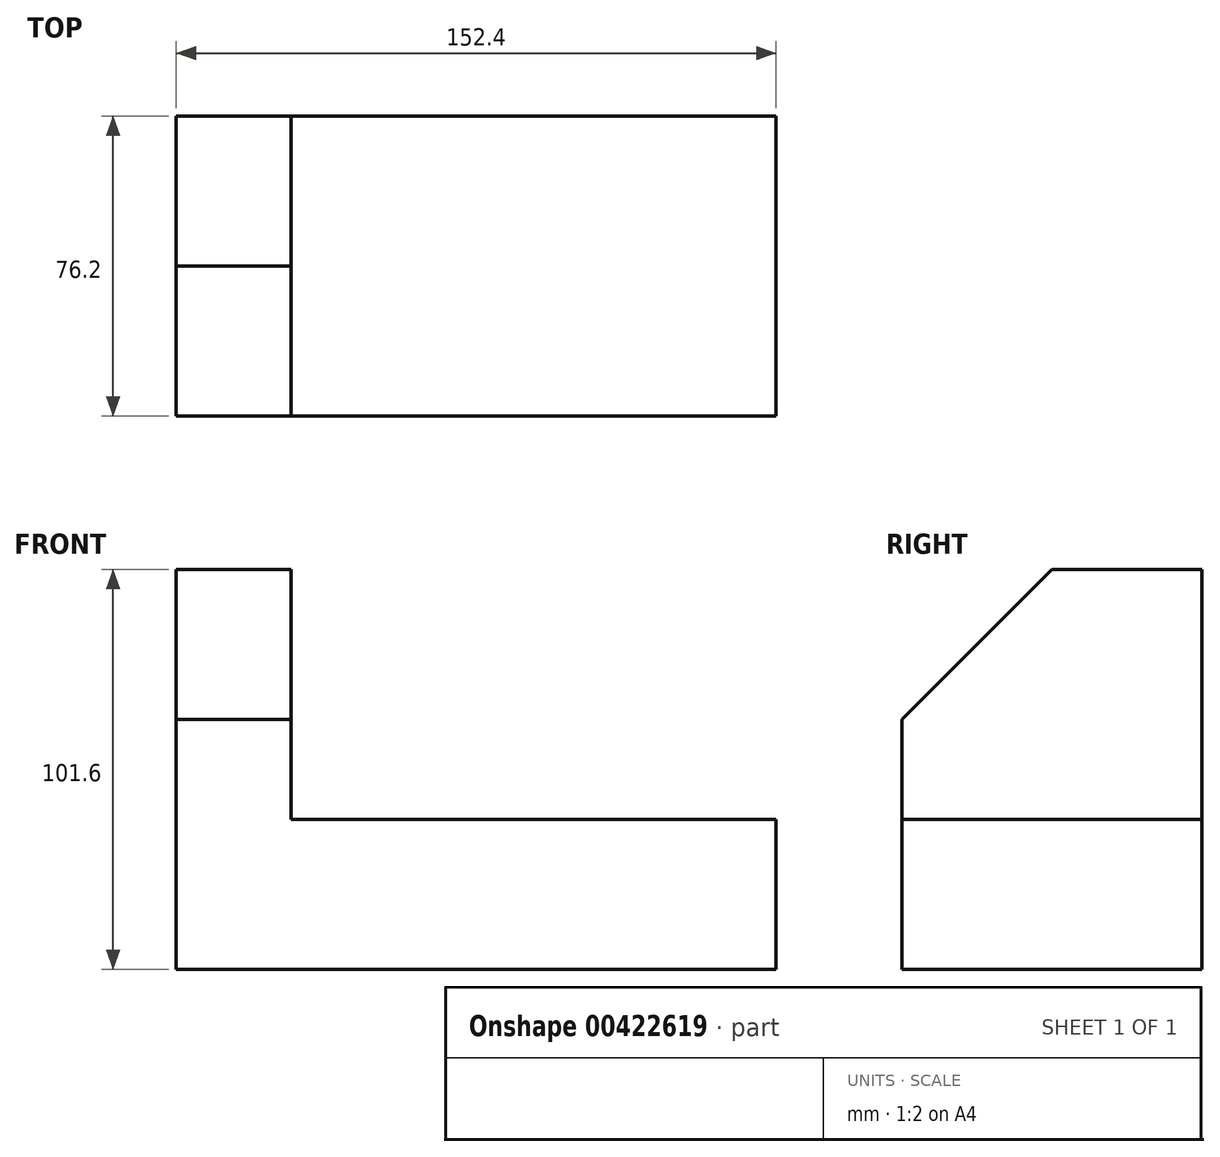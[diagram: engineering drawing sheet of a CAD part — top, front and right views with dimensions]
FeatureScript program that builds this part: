
annotation { "Feature Type Name" : "Feature", "Feature Type Description" : "" }
export const myFeature = defineFeature(function(context is Context, id is Id, definition is map)
    precondition{}
    {
        {
            var Q0;
            Q0=qCreatedBy(makeId("Front.planeOp"),FACE);
            var sketch = newSketch(context, id + "F0", { "sketchPlane" : qUnion([Q0])});
            skLineSegment(sketch, "E0", {"start": v(0, 0) * mm, "end": v(152.4, 0) * mm});
            skLineSegment(sketch, "E1", {"start": v(152.4, 0) * mm, "end": v(152.4, 38.1) * mm});
            skLineSegment(sketch, "E2", {"start": v(152.4, 38.1) * mm, "end": v(29.21, 38.1) * mm});
            skLineSegment(sketch, "E3", {"start": v(29.21, 38.1) * mm, "end": v(29.21, 101.6) * mm});
            skLineSegment(sketch, "E4", {"start": v(29.21, 101.6) * mm, "end": v(0, 101.6) * mm});
            skLineSegment(sketch, "E5", {"start": v(0, 101.6) * mm, "end": v(0, 0) * mm});
            skSolve(sketch);
        }
        {
            var Q0;
            Q0=makeQuery(id+"F0.imprint","IMPRINT",FACE,{"disambiguationData":[TD([[makeQuery(id+"F0.imprint","IMPRINT",EDGE,{"derivedFrom":sQuery(id+"F0.wireOp",EDGE,"E0")}),1.0]])]});
            extrude(context, id + "F1", {"entities" : qUnion([Q0]), "depth" : 76.2 * mm});
        }
        {
            var Q0;
            Q0=makeQuery(id+"F1.opExtrude","SWEPT_FACE",FACE,{"disambiguationData":[OSD([sQuery(id+"F0.wireOp",EDGE,"E3")])]});
            var sketch = newSketch(context, id + "F2", { "sketchPlane" : qUnion([Q0])});
            skLineSegment(sketch, "E6", {"start": v(-38.1, 101.6) * mm, "end": v(-76.2, 63.5) * mm});
            skLineSegment(sketch, "E7", {"start": v(-76.2, 63.5) * mm, "end": v(-76.2, 101.6) * mm});
            skLineSegment(sketch, "E8", {"start": v(-38.1, 101.6) * mm, "end": v(-76.2, 101.6) * mm});
            skSolve(sketch);
        }
        {
            var Q0;
            Q0 = qSketchRegion(id + "F2", true);
            extrude(context, id + "F3", {"entities" : qUnion([Q0]), "operationType" : NewBodyOperationType.REMOVE, "endBound" : BoundingType.THROUGH_ALL, "oppositeDirection" : true, "depth" : 25.4 * mm});
        }
    });
